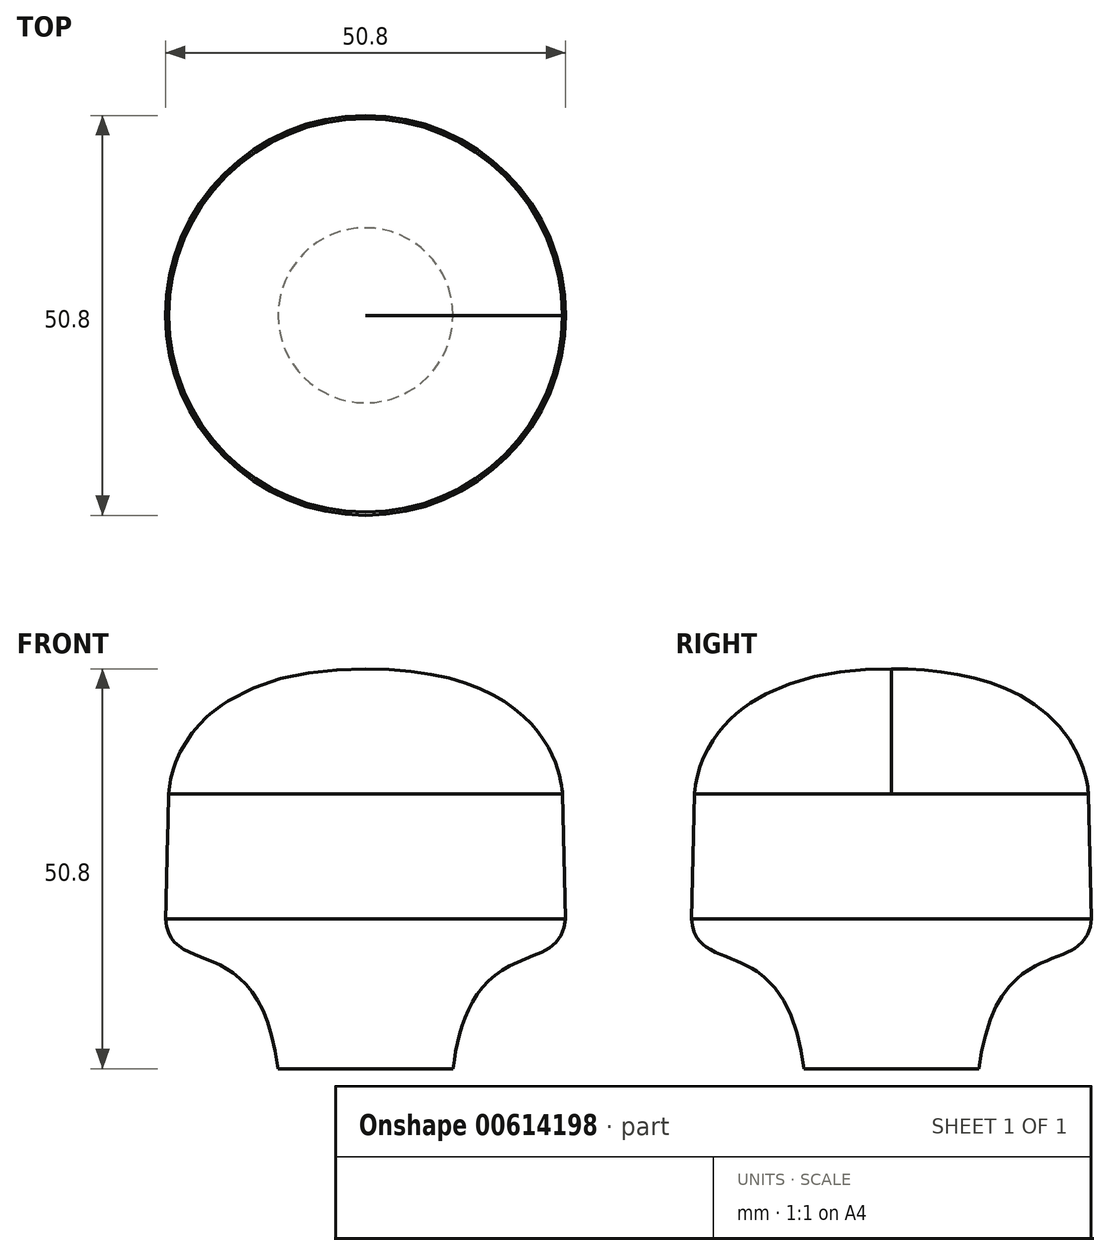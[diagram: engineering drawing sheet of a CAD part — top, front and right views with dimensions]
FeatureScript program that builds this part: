
annotation { "Feature Type Name" : "Feature", "Feature Type Description" : "" }
export const myFeature = defineFeature(function(context is Context, id is Id, definition is map)
    precondition{}
    {
        {
            var Q0;
            Q0=qCreatedBy(makeId("Front.planeOp"),FACE);
            var sketch = newSketch(context, id + "F0", { "sketchPlane" : qUnion([Q0])});
            skLineSegment(sketch, "E0", {"start": v(25.01, -7.39) * mm, "end": v(25.4, -23.26) * mm});
            skLineSegment(sketch, "E1", {"start": v(11.11, -42.3) * mm, "end": v(0, -42.3) * mm});
            skLineSegment(sketch, "E2", {"start": v(0, -42.3) * mm, "end": v(0, 8.5) * mm});
            skFitSpline(sketch, "E3", {"points": [v(0, 8.5) * mm, v(25.01, -7.39) * mm], "startDerivative": vector(72.2, -0.05) * mm, "endDerivative": vector(0.15, -3.25) * mm});
            skFitSpline(sketch, "E4", {"points": [v(11.11, -42.3) * mm, v(25.4, -23.26) * mm], "startDerivative": vector(6.98, 54.53) * mm, "endDerivative": vector(1.64, 23.86) * mm});
            skLineSegment(sketch, "E5", {"start": v(0, 32.74) * mm, "end": v(0, 64) * mm, "construction": true});
            skSolve(sketch);
        }
        {
            var Q0;
            Q0=makeQuery(id+"F0.imprint","IMPRINT",FACE,{"disambiguationData":[TD([[makeQuery(id+"F0.imprint","IMPRINT",EDGE,{"derivedFrom":sQuery(id+"F0.wireOp",EDGE,"E0")}),-1.0]])]});
            var Q1;
            Q1=sQuery(id+"F0.wireOp",EDGE,"E5");
            revolve(context, id + "F1", {"entities" : qUnion([Q0]), "axis" : qUnion([Q1]), "revolveType" : RevolveType.FULL});
        }
    });
